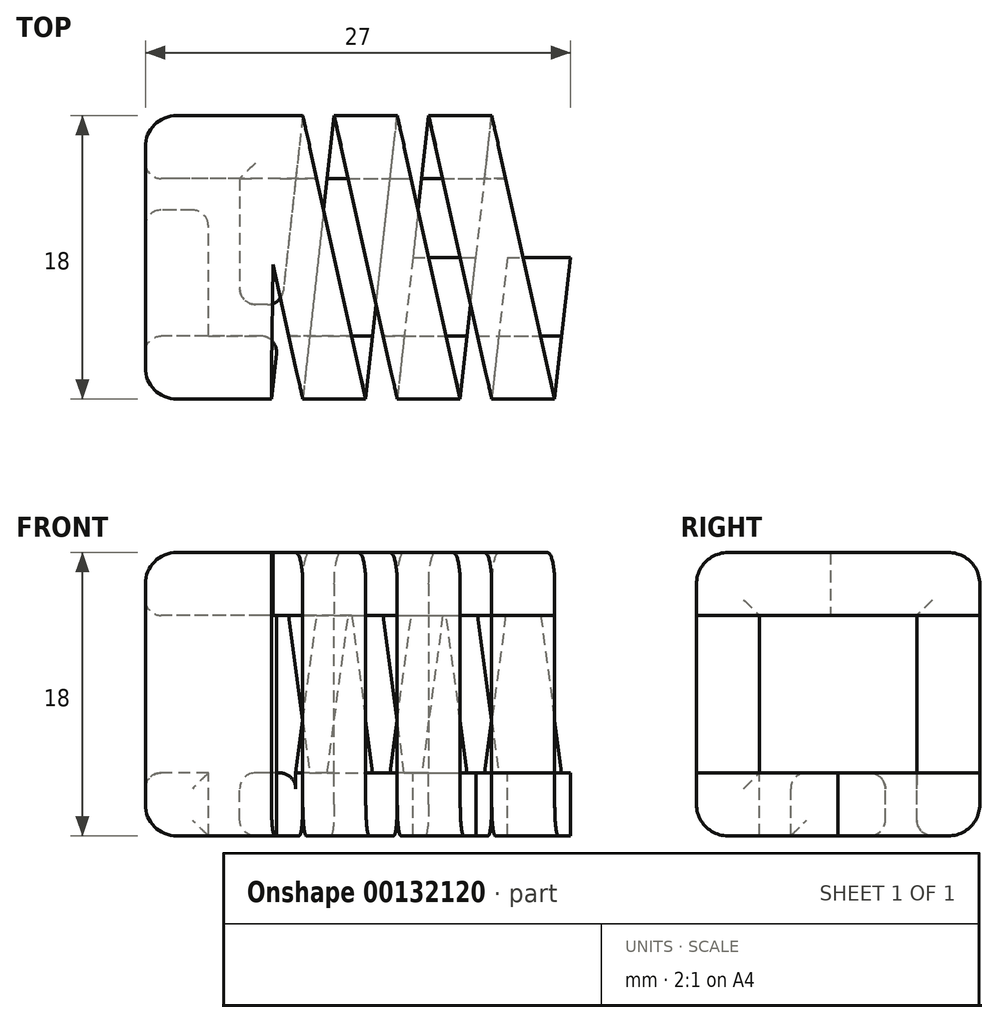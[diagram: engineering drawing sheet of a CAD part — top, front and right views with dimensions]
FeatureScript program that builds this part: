
annotation { "Feature Type Name" : "Feature", "Feature Type Description" : "" }
export const myFeature = defineFeature(function(context is Context, id is Id, definition is map)
    precondition{}
    {
        {
            var Q0;
            Q0=qCreatedBy(makeId("Top.planeOp"),FACE);
            cPlane(context, id + "F0", {"entities" : qUnion([Q0]), "cplaneType" : CPlaneType.OFFSET, "offset" : 10 * mm, "width" : 150 * mm, "height" : 150 * mm});
        }
        {
            var Q0;
            Q0=qCreatedBy(makeId("Top.planeOp"),FACE);
            var sketch = newSketch(context, id + "F1", { "sketchPlane" : qUnion([Q0])});
            skLineSegment(sketch, "E0", {"start": v(0, 0) * mm, "end": v(19.22, 0) * mm, "construction": true});
            skLineSegment(sketch, "E1.0", {"start": v(0, -5) * mm, "end": v(19.22, -5) * mm, "construction": true});
            skLineSegment(sketch, "E2.0", {"start": v(0, 5) * mm, "end": v(19.22, 5) * mm, "construction": true});
            skLineSegment(sketch, "E3.0", {"start": v(0, 9) * mm, "end": v(19.22, 9) * mm, "construction": true});
            skLineSegment(sketch, "E4.0", {"start": v(0, -9) * mm, "end": v(19.22, -9) * mm, "construction": true});
            skLineSegment(sketch, "E5", {"start": v(0, 9) * mm, "end": v(0, -9) * mm, "construction": true});
            skLineSegment(sketch, "E6", {"start": v(0, -9) * mm, "end": v(2, -9) * mm});
            skLineSegment(sketch, "E7", {"start": v(4, 9) * mm, "end": v(2, -9) * mm, "construction": true});
            skLineSegment(sketch, "E8", {"start": v(4, 9) * mm, "end": v(6, 9) * mm, "construction": true});
            skLineSegment(sketch, "E9", {"start": v(6, 9) * mm, "end": v(10, 9) * mm});
            skLineSegment(sketch, "E10", {"start": v(2, -9) * mm, "end": v(4, -9) * mm, "construction": true});
            skLineSegment(sketch, "E11", {"start": v(4, -9) * mm, "end": v(8, -9) * mm});
            skLineSegment(sketch, "E12", {"start": v(6, 9) * mm, "end": v(4, -9) * mm});
            skLineSegment(sketch, "E13", {"start": v(8, -9) * mm, "end": v(10, 9) * mm});
            skLineSegment(sketch, "E14.0", {"start": v(-2, 5) * mm, "end": v(-2, -9) * mm, "construction": true});
            skLineSegment(sketch, "E15.0", {"start": v(-6, 9) * mm, "end": v(-6, -9) * mm, "construction": true});
            skLineSegment(sketch, "E16", {"start": v(0, 5) * mm, "end": v(-6, 5) * mm, "construction": true});
            skLineSegment(sketch, "E17", {"start": v(4, -9) * mm, "end": v(0, -9) * mm, "construction": true});
            skLineSegment(sketch, "E18.0", {"start": v(4, -3) * mm, "end": v(0, -3) * mm, "construction": true});
            skLineSegment(sketch, "E19.0", {"start": v(2, 3) * mm, "end": v(-6, 3) * mm, "construction": true});
            skLineSegment(sketch, "E20", {"start": v(4, 9) * mm, "end": v(2.67, -3) * mm});
            skLineSegment(sketch, "E21", {"start": v(2.67, -3) * mm, "end": v(0, -3) * mm});
            skLineSegment(sketch, "E22", {"start": v(0, 5) * mm, "end": v(0, -3) * mm});
            skLineSegment(sketch, "E23", {"start": v(-6, -9) * mm, "end": v(0, -9) * mm});
            skLineSegment(sketch, "E24", {"start": v(0, -5) * mm, "end": v(-2, -5) * mm});
            skLineSegment(sketch, "E25", {"start": v(-2, -5) * mm, "end": v(-2, 3) * mm});
            skLineSegment(sketch, "E26", {"start": v(-2, 3) * mm, "end": v(-6, 3) * mm});
            skLineSegment(sketch, "E27", {"start": v(0, -5) * mm, "end": v(2.44, -5) * mm});
            skLineSegment(sketch, "E28", {"start": v(2.44, -5) * mm, "end": v(2, -9) * mm});
            skLineSegment(sketch, "E29", {"start": v(-6, 3) * mm, "end": v(-6, -9) * mm});
            skLineSegment(sketch, "E30", {"start": v(-6, 5) * mm, "end": v(-6, 9) * mm});
            skLineSegment(sketch, "E31", {"start": v(0, 5) * mm, "end": v(-6, 5) * mm});
            skLineSegment(sketch, "E32", {"start": v(-6, 9) * mm, "end": v(4, 9) * mm});
            skLineSegment(sketch, "E33", {"start": v(10, 9) * mm, "end": v(12, 9) * mm, "construction": true});
            skLineSegment(sketch, "E34", {"start": v(12, 9) * mm, "end": v(16, 9) * mm});
            skLineSegment(sketch, "E35", {"start": v(8, -9) * mm, "end": v(10, -9) * mm, "construction": true});
            skLineSegment(sketch, "E36", {"start": v(10, -9) * mm, "end": v(14, -9) * mm});
            skLineSegment(sketch, "E37", {"start": v(12, 9) * mm, "end": v(10, -9) * mm});
            skLineSegment(sketch, "E38", {"start": v(14, -9) * mm, "end": v(16, 9) * mm});
            skLineSegment(sketch, "E39", {"start": v(0, 9) * mm, "end": v(0, 5) * mm});
            skLineSegment(sketch, "E40", {"start": v(0, 5) * mm, "end": v(3.56, 5) * mm});
            skLineSegment(sketch, "E41", {"start": v(5.56, 5) * mm, "end": v(9.56, 5) * mm});
            skLineSegment(sketch, "E42", {"start": v(4.44, -5) * mm, "end": v(8.44, -5) * mm});
            skLineSegment(sketch, "E43", {"start": v(11.56, 5) * mm, "end": v(15.56, 5) * mm});
            skLineSegment(sketch, "E44", {"start": v(10.44, -5) * mm, "end": v(14.44, -5) * mm});
            skLineSegment(sketch, "E45", {"start": v(-2, -5) * mm, "end": v(-6, -5) * mm});
            skLineSegment(sketch, "E46", {"start": v(11, 0) * mm, "end": v(15, 0) * mm});
            skPoint(sketch, "E47", {"position": v(13, 0) * mm});
            skPoint(sketch, "E48", {"position": v(-6, 0) * mm});
            skLineSegment(sketch, "E49", {"start": v(5, 0) * mm, "end": v(9, 0) * mm, "construction": true});
            skPoint(sketch, "E50", {"position": v(7, 0) * mm});
            skLineSegment(sketch, "E51", {"start": v(19.22, 9) * mm, "end": v(19.22, -9) * mm});
            skSolve(sketch);
        }
        {
            var Q0;
            Q0=qCreatedBy(id+"F0.planeOp",FACE);
            var sketch = newSketch(context, id + "F2", { "sketchPlane" : qUnion([Q0])});
            skLineSegment(sketch, "E52.0", {"start": v(-6, 9) * mm, "end": v(4, 9) * mm, "construction": true});
            skLineSegment(sketch, "E53.0", {"start": v(-6, 5) * mm, "end": v(-6, 9) * mm, "construction": true});
            skLineSegment(sketch, "E54.0", {"start": v(-6, 9) * mm, "end": v(-6, -9) * mm, "construction": true});
            skLineSegment(sketch, "E55.0", {"start": v(-6, -9) * mm, "end": v(0, -9) * mm, "construction": true});
            skLineSegment(sketch, "E56.0", {"start": v(0, -9) * mm, "end": v(2, -9) * mm, "construction": true});
            skLineSegment(sketch, "E57.0", {"start": v(4, -9) * mm, "end": v(0, -9) * mm, "construction": true});
            skLineSegment(sketch, "E58.0", {"start": v(0, -9) * mm, "end": v(19.22, -9) * mm, "construction": true});
            skLineSegment(sketch, "E59.0", {"start": v(0, 9) * mm, "end": v(19.22, 9) * mm, "construction": true});
            skLineSegment(sketch, "E60.0", {"start": v(14, -9) * mm, "end": v(16, 9) * mm, "construction": true});
            skLineSegment(sketch, "E61.0", {"start": v(12, 9) * mm, "end": v(16, 9) * mm, "construction": true});
            skLineSegment(sketch, "E62.0", {"start": v(12, 9) * mm, "end": v(10, -9) * mm, "construction": true});
            skLineSegment(sketch, "E63.0", {"start": v(10, -9) * mm, "end": v(14, -9) * mm, "construction": true});
            skLineSegment(sketch, "E64.0", {"start": v(8, -9) * mm, "end": v(10, 9) * mm, "construction": true});
            skLineSegment(sketch, "E65.0", {"start": v(4, 9) * mm, "end": v(2.67, -3) * mm, "construction": true});
            skLineSegment(sketch, "E66.0", {"start": v(2.44, -5) * mm, "end": v(2, -9) * mm, "construction": true});
            skLineSegment(sketch, "E67", {"start": v(10, 9) * mm, "end": v(14, -9) * mm});
            skLineSegment(sketch, "E68", {"start": v(10, 9) * mm, "end": v(6, 9) * mm});
            skLineSegment(sketch, "E69", {"start": v(6, 9) * mm, "end": v(10, -9) * mm});
            skLineSegment(sketch, "E70", {"start": v(14, -9) * mm, "end": v(10, -9) * mm});
            skLineSegment(sketch, "E71", {"start": v(4, 9) * mm, "end": v(8, -9) * mm});
            skLineSegment(sketch, "E72", {"start": v(8, -9) * mm, "end": v(4, -9) * mm});
            skLineSegment(sketch, "E73", {"start": v(4, 9) * mm, "end": v(-6, 9) * mm});
            skLineSegment(sketch, "E74", {"start": v(-6, 9) * mm, "end": v(-6, -9) * mm});
            skLineSegment(sketch, "E75", {"start": v(-6, -9) * mm, "end": v(2, -9) * mm});
            skLineSegment(sketch, "E76", {"start": v(2, -9) * mm, "end": v(2.1, -0.47) * mm});
            skPoint(sketch, "E76.endSnap0", {"position": v(2.22, -7) * mm});
            skLineSegment(sketch, "E77", {"start": v(4, -9) * mm, "end": v(2.1, -0.47) * mm});
            skPoint(sketch, "E78.orphan", {"position": v(2.22, 9) * mm});
            skLineSegment(sketch, "E79.0", {"start": v(0, 5) * mm, "end": v(19.22, 5) * mm, "construction": true});
            skLineSegment(sketch, "E80.0", {"start": v(0, -5) * mm, "end": v(19.22, -5) * mm, "construction": true});
            skLineSegment(sketch, "E81", {"start": v(6.89, 5) * mm, "end": v(10.89, 5) * mm});
            skLineSegment(sketch, "E82", {"start": v(9.11, -5) * mm, "end": v(13.11, -5) * mm});
            skLineSegment(sketch, "E83", {"start": v(7.11, -5) * mm, "end": v(3.11, -5) * mm});
            skLineSegment(sketch, "E84", {"start": v(0, 9) * mm, "end": v(0, 5) * mm});
            skLineSegment(sketch, "E85", {"start": v(0, 5) * mm, "end": v(4.89, 5) * mm});
            skLineSegment(sketch, "E86", {"start": v(-30.78, 9) * mm, "end": v(-30.78, -9) * mm, "construction": true});
            skLineSegment(sketch, "E87", {"start": v(19.22, 9) * mm, "end": v(19.22, -9) * mm, "construction": true});
            skSolve(sketch);
        }
        {
            var Q0;
            {var subQ4=sQuery(id+"F1.wireOp",EDGE,"E39");Q0=makeQuery(id+"F1.imprint","IMPRINT",FACE,{"disambiguationData":[TD([[makeQuery(id+"F1.imprint","IMPRINT",EDGE,{"derivedFrom":subQ4}),1.0]])]});}
            var Q1;
            {var subQ0=sQuery(id+"F1.wireOp",EDGE,"E21");Q1=makeQuery(id+"F1.imprint","IMPRINT",FACE,{"disambiguationData":[TD([[makeQuery(id+"F1.imprint","IMPRINT",EDGE,{"derivedFrom":subQ0}),-1.0]])]});}
            var Q2;
            {var subQ0=sQuery(id+"F1.wireOp",EDGE,"E41");Q2=makeQuery(id+"F1.imprint","IMPRINT",FACE,{"disambiguationData":[TD([[makeQuery(id+"F1.imprint","IMPRINT",EDGE,{"derivedFrom":subQ0}),-1.0]])]});}
            var Q3;
            {var subQ0=sQuery(id+"F1.wireOp",EDGE,"E9");Q3=makeQuery(id+"F1.imprint","IMPRINT",FACE,{"disambiguationData":[TD([[makeQuery(id+"F1.imprint","IMPRINT",EDGE,{"derivedFrom":subQ0}),-1.0]])]});}
            var Q4;
            {var subQ0=sQuery(id+"F1.wireOp",EDGE,"E11");Q4=makeQuery(id+"F1.imprint","IMPRINT",FACE,{"disambiguationData":[TD([[makeQuery(id+"F1.imprint","IMPRINT",EDGE,{"derivedFrom":subQ0}),1.0]])]});}
            var Q5;
            {var subQ0=sQuery(id+"F1.wireOp",EDGE,"E36");Q5=makeQuery(id+"F1.imprint","IMPRINT",FACE,{"disambiguationData":[TD([[makeQuery(id+"F1.imprint","IMPRINT",EDGE,{"derivedFrom":subQ0}),1.0]])]});}
            var Q6;
            Q6=makeQuery(id+"F1.imprint","IMPRINT",FACE,{"disambiguationData":[TD([[makeQuery(id+"F1.imprint","IMPRINT",EDGE,{"derivedFrom":sQuery(id+"F1.wireOp",EDGE,"E25")}),1.0]])]});
            var Q7;
            Q7=makeQuery(id+"F1.imprint","IMPRINT",FACE,{"disambiguationData":[TD([[makeQuery(id+"F1.imprint","IMPRINT",EDGE,{"derivedFrom":sQuery(id+"F1.wireOp",EDGE,"E6")}),1.0]])]});
            var Q8;
            {var subQ0=sQuery(id+"F1.wireOp",EDGE,"E30");Q8=makeQuery(id+"F1.imprint","IMPRINT",FACE,{"disambiguationData":[TD([[makeQuery(id+"F1.imprint","IMPRINT",EDGE,{"derivedFrom":subQ0}),-1.0]])]});}
            var Q9;
            {var subQ0=sQuery(id+"F1.wireOp",EDGE,"E44");Q9=makeQuery(id+"F1.imprint","IMPRINT",FACE,{"disambiguationData":[TD([[makeQuery(id+"F1.imprint","IMPRINT",EDGE,{"derivedFrom":subQ0}),1.0]])]});}
            extrude(context, id + "F3", {"entities" : qUnion([Q0, Q1, Q2, Q3, Q4, Q5, Q6, Q7, Q8, Q9]), "oppositeDirection" : true, "depth" : 4 * mm});
        }
        {
            var Q0;
            {var subQ0=sQuery(id+"F2.wireOp",EDGE,"E74");Q0=makeQuery(id+"F2.imprint","IMPRINT",FACE,{"disambiguationData":[TD([[makeQuery(id+"F2.imprint","IMPRINT",EDGE,{"derivedFrom":subQ0}),1.0]])]});}
            var Q1;
            {var subQ4=sQuery(id+"F2.wireOp",EDGE,"E84");Q1=makeQuery(id+"F2.imprint","IMPRINT",FACE,{"disambiguationData":[TD([[makeQuery(id+"F2.imprint","IMPRINT",EDGE,{"derivedFrom":subQ4}),1.0]])]});}
            var Q2;
            {var subQ0=sQuery(id+"F2.wireOp",EDGE,"E68");Q2=makeQuery(id+"F2.imprint","IMPRINT",FACE,{"disambiguationData":[TD([[makeQuery(id+"F2.imprint","IMPRINT",EDGE,{"derivedFrom":subQ0}),1.0]])]});}
            var Q3;
            {var subQ0=sQuery(id+"F2.wireOp",EDGE,"E81");Q3=makeQuery(id+"F2.imprint","IMPRINT",FACE,{"disambiguationData":[TD([[makeQuery(id+"F2.imprint","IMPRINT",EDGE,{"derivedFrom":subQ0}),-1.0]])]});}
            var Q4;
            {var subQ0=sQuery(id+"F2.wireOp",EDGE,"E70");Q4=makeQuery(id+"F2.imprint","IMPRINT",FACE,{"disambiguationData":[TD([[makeQuery(id+"F2.imprint","IMPRINT",EDGE,{"derivedFrom":subQ0}),-1.0]])]});}
            var Q5;
            {var subQ0=sQuery(id+"F2.wireOp",EDGE,"E72");Q5=makeQuery(id+"F2.imprint","IMPRINT",FACE,{"disambiguationData":[TD([[makeQuery(id+"F2.imprint","IMPRINT",EDGE,{"derivedFrom":subQ0}),-1.0]])]});}
            extrude(context, id + "F4", {"entities" : qUnion([Q0, Q1, Q2, Q3, Q4, Q5]), "depth" : 4 * mm});
        }
        {
            var Q0;
            {var subQ0=sQuery(id+"F1.wireOp",EDGE,"E30");Q0=makeQuery(id+"F1.imprint","IMPRINT",FACE,{"disambiguationData":[TD([[makeQuery(id+"F1.imprint","IMPRINT",EDGE,{"derivedFrom":subQ0}),-1.0]])]});}
            var Q1;
            Q1=makeQuery(id+"F1.imprint","IMPRINT",FACE,{"disambiguationData":[TD([[makeQuery(id+"F1.imprint","IMPRINT",EDGE,{"derivedFrom":sQuery(id+"F1.wireOp",EDGE,"E6")}),1.0]])]});
            extrude(context, id + "F5", {"entities" : qUnion([Q0, Q1]), "depth" : 10 * mm});
        }
        {
            var Q0;
            {var subQ0=sQuery(id+"F2.wireOp",EDGE,"E72");Q0=makeQuery(id+"F2.imprint","IMPRINT",FACE,{"disambiguationData":[TD([[makeQuery(id+"F2.imprint","IMPRINT",EDGE,{"derivedFrom":subQ0}),-1.0]])]});}
            var Q1;
            {var subQ0=sQuery(id+"F1.wireOp",EDGE,"E11");Q1=makeQuery(id+"F1.imprint","IMPRINT",FACE,{"disambiguationData":[TD([[makeQuery(id+"F1.imprint","IMPRINT",EDGE,{"derivedFrom":subQ0}),1.0]])]});}
            loft(context, id + "F6", {"sheetProfilesArray" : [{ "sheetProfileEntities" : qUnion([Q0]) }, { "sheetProfileEntities" : qUnion([Q1]) }]});
        }
        {
            var Q0;
            {var subQ0=sQuery(id+"F1.wireOp",EDGE,"E9");Q0=makeQuery(id+"F1.imprint","IMPRINT",FACE,{"disambiguationData":[TD([[makeQuery(id+"F1.imprint","IMPRINT",EDGE,{"derivedFrom":subQ0}),-1.0]])]});}
            var Q1;
            {var subQ0=sQuery(id+"F2.wireOp",EDGE,"E68");Q1=makeQuery(id+"F2.imprint","IMPRINT",FACE,{"disambiguationData":[TD([[makeQuery(id+"F2.imprint","IMPRINT",EDGE,{"derivedFrom":subQ0}),1.0]])]});}
            loft(context, id + "F7", {"sheetProfilesArray" : [{ "sheetProfileEntities" : qUnion([Q0]) }, { "sheetProfileEntities" : qUnion([Q1]) }]});
        }
        {
            var Q0;
            {var subQ0=sQuery(id+"F1.wireOp",EDGE,"E36");Q0=makeQuery(id+"F1.imprint","IMPRINT",FACE,{"disambiguationData":[TD([[makeQuery(id+"F1.imprint","IMPRINT",EDGE,{"derivedFrom":subQ0}),1.0]])]});}
            var Q1;
            {var subQ0=sQuery(id+"F2.wireOp",EDGE,"E70");Q1=makeQuery(id+"F2.imprint","IMPRINT",FACE,{"disambiguationData":[TD([[makeQuery(id+"F2.imprint","IMPRINT",EDGE,{"derivedFrom":subQ0}),-1.0]])]});}
            loft(context, id + "F8", {"sheetProfilesArray" : [{ "sheetProfileEntities" : qUnion([Q0]) }, { "sheetProfileEntities" : qUnion([Q1]) }]});
        }
        {
            var Q0;
            {var subQ4=sQuery(id+"F1.wireOp",EDGE,"E39");Q0=makeQuery(id+"F1.imprint","IMPRINT",FACE,{"disambiguationData":[TD([[makeQuery(id+"F1.imprint","IMPRINT",EDGE,{"derivedFrom":subQ4}),1.0]])]});}
            var Q1;
            {var subQ4=sQuery(id+"F2.wireOp",EDGE,"E84");Q1=makeQuery(id+"F2.imprint","IMPRINT",FACE,{"disambiguationData":[TD([[makeQuery(id+"F2.imprint","IMPRINT",EDGE,{"derivedFrom":subQ4}),1.0]])]});}
            loft(context, id + "F9", {"sheetProfilesArray" : [{ "sheetProfileEntities" : qUnion([Q0]) }, { "sheetProfileEntities" : qUnion([Q1]) }]});
        }
        {
            var Q0;
            Q0=makeQuery(id+"F3.opExtrude","SWEPT_BODY",BODY,{"disambiguationData":[OSD([sQuery(id+"F1.wireOp",EDGE,"E9"),sQuery(id+"F1.wireOp",EDGE,"E11"),sQuery(id+"F1.wireOp",EDGE,"E12"),sQuery(id+"F1.wireOp",EDGE,"E13")])]});
            var Q1;
            Q1=makeQuery(id+"F3.opExtrude","SWEPT_BODY",BODY,{"disambiguationData":[OSD([sQuery(id+"F1.wireOp",EDGE,"E34"),sQuery(id+"F1.wireOp",EDGE,"E36"),sQuery(id+"F1.wireOp",EDGE,"E37"),sQuery(id+"F1.wireOp",EDGE,"E38")])]});
            var Q2;
            Q2=makeQuery(id+"F4.opExtrude","SWEPT_BODY",BODY,{"disambiguationData":[OSD([sQuery(id+"F2.wireOp",EDGE,"E71"),sQuery(id+"F2.wireOp",EDGE,"E72"),sQuery(id+"F2.wireOp",EDGE,"E73"),sQuery(id+"F2.wireOp",EDGE,"E74"),sQuery(id+"F2.wireOp",EDGE,"E75"),sQuery(id+"F2.wireOp",EDGE,"E76"),sQuery(id+"F2.wireOp",EDGE,"E77")])]});
            var Q3;
            Q3=makeQuery(id+"F3.opExtrude","SWEPT_BODY",BODY,{"disambiguationData":[OSD([sQuery(id+"F1.wireOp",EDGE,"E20"),sQuery(id+"F1.wireOp",EDGE,"E21"),sQuery(id+"F1.wireOp",EDGE,"E22"),sQuery(id+"F1.wireOp",EDGE,"E30"),sQuery(id+"F1.wireOp",EDGE,"E31"),sQuery(id+"F1.wireOp",EDGE,"E32")])]});
            var Q4;
            Q4=makeQuery(id+"F4.opExtrude","SWEPT_BODY",BODY,{"disambiguationData":[OSD([sQuery(id+"F2.wireOp",EDGE,"E67"),sQuery(id+"F2.wireOp",EDGE,"E68"),sQuery(id+"F2.wireOp",EDGE,"E69"),sQuery(id+"F2.wireOp",EDGE,"E70")])]});
            var Q5;
            Q5=makeQuery(id+"F3.opExtrude","SWEPT_BODY",BODY,{"disambiguationData":[OSD([sQuery(id+"F1.wireOp",EDGE,"E6"),sQuery(id+"F1.wireOp",EDGE,"E23"),sQuery(id+"F1.wireOp",EDGE,"E24"),sQuery(id+"F1.wireOp",EDGE,"E25"),sQuery(id+"F1.wireOp",EDGE,"E26"),sQuery(id+"F1.wireOp",EDGE,"E27"),sQuery(id+"F1.wireOp",EDGE,"E28"),sQuery(id+"F1.wireOp",EDGE,"E29")])]});
            var Q6;
            {var subQ0=sQuery(id+"F2.wireOp",EDGE,"E70");var subQ4=sQuery(id+"F1.wireOp",EDGE,"E36");Q6=makeQuery(id+"F8.opLoft","SWEPT_BODY",BODY,{"disambiguationData":[OSD([makeQuery(id+"F1.imprint","IMPRINT",FACE,{"disambiguationData":[TD([[makeQuery(id+"F1.imprint","IMPRINT",EDGE,{"derivedFrom":subQ4}),1.0]])]}),makeQuery(id+"F2.imprint","IMPRINT",FACE,{"disambiguationData":[TD([[makeQuery(id+"F2.imprint","IMPRINT",EDGE,{"derivedFrom":subQ0}),-1.0]])]})])]});}
            var Q7;
            {var subQ0=sQuery(id+"F2.wireOp",EDGE,"E72");var subQ4=sQuery(id+"F1.wireOp",EDGE,"E11");Q7=makeQuery(id+"F6.opLoft","SWEPT_BODY",BODY,{"disambiguationData":[OSD([makeQuery(id+"F1.imprint","IMPRINT",FACE,{"disambiguationData":[TD([[makeQuery(id+"F1.imprint","IMPRINT",EDGE,{"derivedFrom":subQ4}),1.0]])]}),makeQuery(id+"F2.imprint","IMPRINT",FACE,{"disambiguationData":[TD([[makeQuery(id+"F2.imprint","IMPRINT",EDGE,{"derivedFrom":subQ0}),-1.0]])]})])]});}
            var Q8;
            {var subQ0=sQuery(id+"F2.wireOp",EDGE,"E68");var subQ4=sQuery(id+"F1.wireOp",EDGE,"E9");Q8=makeQuery(id+"F7.opLoft","SWEPT_BODY",BODY,{"disambiguationData":[OSD([makeQuery(id+"F1.imprint","IMPRINT",FACE,{"disambiguationData":[TD([[makeQuery(id+"F1.imprint","IMPRINT",EDGE,{"derivedFrom":subQ4}),-1.0]])]}),makeQuery(id+"F2.imprint","IMPRINT",FACE,{"disambiguationData":[TD([[makeQuery(id+"F2.imprint","IMPRINT",EDGE,{"derivedFrom":subQ0}),1.0]])]})])]});}
            var Q9;
            Q9=makeQuery(id+"F5.opExtrude","SWEPT_BODY",BODY,{"disambiguationData":[OSD([sQuery(id+"F1.wireOp",EDGE,"E30"),sQuery(id+"F1.wireOp",EDGE,"E31"),sQuery(id+"F1.wireOp",EDGE,"E32"),sQuery(id+"F1.wireOp",EDGE,"E39")])]});
            var Q10;
            {var subQ4=sQuery(id+"F2.wireOp",EDGE,"E84");var subQ9=sQuery(id+"F1.wireOp",EDGE,"E39");Q10=makeQuery(id+"F9.opLoft","SWEPT_BODY",BODY,{"disambiguationData":[OSD([makeQuery(id+"F1.imprint","IMPRINT",FACE,{"disambiguationData":[TD([[makeQuery(id+"F1.imprint","IMPRINT",EDGE,{"derivedFrom":subQ9}),1.0]])]}),makeQuery(id+"F2.imprint","IMPRINT",FACE,{"disambiguationData":[TD([[makeQuery(id+"F2.imprint","IMPRINT",EDGE,{"derivedFrom":subQ4}),1.0]])]})])]});}
            var Q11;
            Q11=makeQuery(id+"F5.opExtrude","SWEPT_BODY",BODY,{"disambiguationData":[OSD([sQuery(id+"F1.wireOp",EDGE,"E6"),sQuery(id+"F1.wireOp",EDGE,"E23"),sQuery(id+"F1.wireOp",EDGE,"E24"),sQuery(id+"F1.wireOp",EDGE,"E27"),sQuery(id+"F1.wireOp",EDGE,"E28"),sQuery(id+"F1.wireOp",EDGE,"E29"),sQuery(id+"F1.wireOp",EDGE,"E45")])]});
            booleanBodies(context, id + "F10", {"operationType" : BooleanOperationType.UNION, "tools" : qUnion([Q0, Q1, Q2, Q3, Q4, Q5, Q6, Q7, Q8, Q9, Q10, Q11])});
        }
        {
            var Q0;
            Q0=makeQuery(id+"F4.opExtrude","CAP_EDGE",EDGE,{"disambiguationData":[OSD([sQuery(id+"F2.wireOp",EDGE,"E68")])],"isStart":false});
            var Q1;
            Q1=makeQuery(id+"F4.opExtrude","CAP_EDGE",EDGE,{"disambiguationData":[OSD([sQuery(id+"F2.wireOp",EDGE,"E73")])],"isStart":false});
            var Q2;
            Q2=makeQuery(id+"F5.opExtrude","SWEPT_EDGE",EDGE,{"disambiguationData":[OSD([sQuery(id+"F1.wireOp",EDGE,"E30"),sQuery(id+"F1.wireOp",EDGE,"E32")])]});
            var Q3;
            Q3=makeQuery(id+"F4.opExtrude","SWEPT_EDGE",EDGE,{"disambiguationData":[OSD([sQuery(id+"F2.wireOp",EDGE,"E73"),sQuery(id+"F2.wireOp",EDGE,"E74")])]});
            var Q4;
            Q4=makeQuery(id+"F4.opExtrude","CAP_EDGE",EDGE,{"disambiguationData":[OSD([sQuery(id+"F2.wireOp",EDGE,"E74")])],"isStart":false});
            var Q5;
            Q5=makeQuery(id+"F4.opExtrude","CAP_EDGE",EDGE,{"disambiguationData":[OSD([sQuery(id+"F2.wireOp",EDGE,"E75")])],"isStart":false});
            var Q6;
            Q6=makeQuery(id+"F4.opExtrude","CAP_EDGE",EDGE,{"disambiguationData":[OSD([sQuery(id+"F2.wireOp",EDGE,"E72")])],"isStart":false});
            var Q7;
            Q7=makeQuery(id+"F4.opExtrude","CAP_EDGE",EDGE,{"disambiguationData":[OSD([sQuery(id+"F2.wireOp",EDGE,"E70")])],"isStart":false});
            var Q8;
            Q8=makeQuery(id+"F5.opExtrude","SWEPT_EDGE",EDGE,{"disambiguationData":[OSD([sQuery(id+"F1.wireOp",EDGE,"E23"),sQuery(id+"F1.wireOp",EDGE,"E29")])]});
            var Q9;
            Q9=makeQuery(id+"F4.opExtrude","SWEPT_EDGE",EDGE,{"disambiguationData":[OSD([sQuery(id+"F2.wireOp",EDGE,"E74"),sQuery(id+"F2.wireOp",EDGE,"E75")])]});
            var Q10;
            Q10=makeQuery(id+"F3.opExtrude","SWEPT_EDGE",EDGE,{"disambiguationData":[OSD([sQuery(id+"F1.wireOp",EDGE,"E30"),sQuery(id+"F1.wireOp",EDGE,"E32")])]});
            var Q11;
            Q11=makeQuery(id+"F3.opExtrude","SWEPT_EDGE",EDGE,{"disambiguationData":[OSD([sQuery(id+"F1.wireOp",EDGE,"E23"),sQuery(id+"F1.wireOp",EDGE,"E29")])]});
            var Q12;
            Q12=makeQuery(id+"F3.opExtrude","CAP_EDGE",EDGE,{"disambiguationData":[OSD([sQuery(id+"F1.wireOp",EDGE,"E29")])],"isStart":false});
            var Q13;
            Q13=makeQuery(id+"F3.opExtrude","CAP_EDGE",EDGE,{"disambiguationData":[OSD([sQuery(id+"F1.wireOp",EDGE,"E30")])],"isStart":false});
            var Q14;
            Q14=makeQuery(id+"F3.opExtrude","CAP_EDGE",EDGE,{"disambiguationData":[OSD([sQuery(id+"F1.wireOp",EDGE,"E6"),sQuery(id+"F1.wireOp",EDGE,"E23")])],"isStart":false});
            var Q15;
            Q15=makeQuery(id+"F3.opExtrude","CAP_EDGE",EDGE,{"disambiguationData":[OSD([sQuery(id+"F1.wireOp",EDGE,"E32")])],"isStart":false});
            var Q16;
            Q16=makeQuery(id+"F3.opExtrude","CAP_EDGE",EDGE,{"disambiguationData":[OSD([sQuery(id+"F1.wireOp",EDGE,"E11")])],"isStart":false});
            var Q17;
            Q17=makeQuery(id+"F3.opExtrude","CAP_EDGE",EDGE,{"disambiguationData":[OSD([sQuery(id+"F1.wireOp",EDGE,"E36")])],"isStart":false});
            var Q18;
            Q18=makeQuery(id+"F3.opExtrude","CAP_EDGE",EDGE,{"disambiguationData":[OSD([sQuery(id+"F1.wireOp",EDGE,"E9")])],"isStart":false});
            fillet(context, id + "F11", {"entities" : qUnion([Q0, Q1, Q2, Q3, Q4, Q5, Q6, Q7, Q8, Q9, Q10, Q11, Q12, Q13, Q14, Q15, Q16, Q17, Q18]), "radius" : 2 * mm, "tangentPropagation" : true, "allowEdgeOverflow" : false});
        }
        {
            var Q0;
            Q0=makeQuery(id+"F3.opExtrude","CAP_EDGE",EDGE,{"disambiguationData":[OSD([sQuery(id+"F1.wireOp",EDGE,"E29")])],"isStart":true});
            var Q1;
            Q1=makeQuery(id+"F5.opExtrude","SWEPT_EDGE",EDGE,{"disambiguationData":[OSD([sQuery(id+"F1.wireOp",EDGE,"E29"),sQuery(id+"F1.wireOp",EDGE,"E45")])]});
            var Q2;
            Q2=makeQuery(id+"F4.opExtrude","CAP_EDGE",EDGE,{"disambiguationData":[OSD([sQuery(id+"F2.wireOp",EDGE,"E74")])],"isStart":true});
            var Q3;
            {var subQ0=sQuery(id+"F1.wireOp",EDGE,"E31");var subQ1=sQuery(id+"F1.wireOp",EDGE,"E30");Q3=makeQuery(id+"F10.opBoolean","MERGE",EDGE,{"derivedFrom":[makeQuery(id+"F3.opExtrude","SWEPT_EDGE",EDGE,{"disambiguationData":[OSD([subQ1,subQ0])]}),makeQuery(id+"F5.opExtrude","SWEPT_EDGE",EDGE,{"disambiguationData":[OSD([subQ1,subQ0])]})]});}
            var Q4;
            Q4=makeQuery(id+"F3.opExtrude","SWEPT_EDGE",EDGE,{"disambiguationData":[OSD([sQuery(id+"F1.wireOp",EDGE,"E26"),sQuery(id+"F1.wireOp",EDGE,"E29")])]});
            var Q5;
            Q5=makeQuery(id+"F3.opExtrude","CAP_EDGE",EDGE,{"disambiguationData":[OSD([sQuery(id+"F1.wireOp",EDGE,"E26")])],"isStart":true});
            var Q6;
            Q6=makeQuery(id+"F3.opExtrude","SWEPT_EDGE",EDGE,{"disambiguationData":[OSD([sQuery(id+"F1.wireOp",EDGE,"E25"),sQuery(id+"F1.wireOp",EDGE,"E26")])]});
            var Q7;
            Q7=makeQuery(id+"F3.opExtrude","CAP_EDGE",EDGE,{"disambiguationData":[OSD([sQuery(id+"F1.wireOp",EDGE,"E22")])],"isStart":true});
            var Q8;
            Q8=makeQuery(id+"F3.opExtrude","CAP_EDGE",EDGE,{"disambiguationData":[OSD([sQuery(id+"F1.wireOp",EDGE,"E22")])],"isStart":false});
            var Q9;
            Q9=makeQuery(id+"F3.opExtrude","CAP_EDGE",EDGE,{"disambiguationData":[OSD([sQuery(id+"F1.wireOp",EDGE,"E21")])],"isStart":true});
            var Q10;
            Q10=makeQuery(id+"F10.opBoolean","SPLIT",EDGE,{"derivedFrom":makeQuery(id+"F3.opExtrude","CAP_EDGE",EDGE,{"disambiguationData":[OSD([sQuery(id+"F1.wireOp",EDGE,"E20")])],"isStart":true})});
            var Q11;
            Q11=makeQuery(id+"F3.opExtrude","SWEPT_EDGE",EDGE,{"disambiguationData":[OSD([sQuery(id+"F1.wireOp",EDGE,"E20"),sQuery(id+"F1.wireOp",EDGE,"E21")])]});
            var Q12;
            Q12=makeQuery(id+"F3.opExtrude","SWEPT_EDGE",EDGE,{"disambiguationData":[OSD([sQuery(id+"F1.wireOp",EDGE,"E21"),sQuery(id+"F1.wireOp",EDGE,"E22")])]});
            var Q13;
            {var subQ0=sQuery(id+"F1.wireOp",EDGE,"E28");var subQ1=sQuery(id+"F1.wireOp",EDGE,"E27");Q13=makeQuery(id+"F10.opBoolean","MERGE",EDGE,{"derivedFrom":[makeQuery(id+"F3.opExtrude","SWEPT_EDGE",EDGE,{"disambiguationData":[OSD([subQ1,subQ0])]}),makeQuery(id+"F5.opExtrude","SWEPT_EDGE",EDGE,{"disambiguationData":[OSD([subQ1,subQ0])]})]});}
            fillet(context, id + "F12", {"entities" : qUnion([Q0, Q1, Q2, Q3, Q4, Q5, Q6, Q7, Q8, Q9, Q10, Q11, Q12, Q13]), "radius" : 1 * mm, "tangentPropagation" : true, "allowEdgeOverflow" : false});
        }
        {
            var Q0;
            Q0=qCreatedBy(makeId("Top.planeOp"),FACE);
            var sketch = newSketch(context, id + "F13", { "sketchPlane" : qUnion([Q0])});
            skLineSegment(sketch, "E88.0", {"start": v(0, 9) * mm, "end": v(19.22, 9) * mm, "construction": true});
            skLineSegment(sketch, "E88.1", {"start": v(0, 5) * mm, "end": v(19.22, 5) * mm, "construction": true});
            skLineSegment(sketch, "E89.0", {"start": v(14, -9) * mm, "end": v(16, 9) * mm, "construction": true});
            skLineSegment(sketch, "E90.0", {"start": v(0, -5) * mm, "end": v(19.22, -5) * mm, "construction": true});
            skLineSegment(sketch, "E91.0", {"start": v(0, -9) * mm, "end": v(19.22, -9) * mm, "construction": true});
            skLineSegment(sketch, "E92", {"start": v(16, 9) * mm, "end": v(18, 9) * mm, "construction": true});
            skLineSegment(sketch, "E93", {"start": v(18, 9) * mm, "end": v(22, 9) * mm});
            skLineSegment(sketch, "E94", {"start": v(14, -9) * mm, "end": v(16, -9) * mm, "construction": true});
            skLineSegment(sketch, "E95", {"start": v(16, -9) * mm, "end": v(20, -9) * mm});
            skLineSegment(sketch, "E96", {"start": v(18, 9) * mm, "end": v(16, -9) * mm});
            skLineSegment(sketch, "E97", {"start": v(20, -9) * mm, "end": v(22, 9) * mm});
            skLineSegment(sketch, "E98", {"start": v(17.56, 5) * mm, "end": v(21.56, 5) * mm});
            skLineSegment(sketch, "E99", {"start": v(16.44, -5) * mm, "end": v(20.44, -5) * mm});
            skLineSegment(sketch, "E100", {"start": v(17, 0) * mm, "end": v(21, 0) * mm});
            skLineSegment(sketch, "E101.0", {"start": v(12, 9) * mm, "end": v(10, -9) * mm, "construction": true});
            skLineSegment(sketch, "E102", {"start": v(15, 0) * mm, "end": v(11, 0) * mm, "construction": true});
            skSolve(sketch);
        }
        {
            var Q0;
            Q0=qCreatedBy(id+"F0.planeOp",FACE);
            var sketch = newSketch(context, id + "F14", { "sketchPlane" : qUnion([Q0])});
            skLineSegment(sketch, "E103.0", {"start": v(0, 5) * mm, "end": v(19.22, 5) * mm, "construction": true});
            skLineSegment(sketch, "E104.0", {"start": v(0, 9) * mm, "end": v(19.22, 9) * mm, "construction": true});
            skLineSegment(sketch, "E105.0", {"start": v(0, -5) * mm, "end": v(19.22, -5) * mm, "construction": true});
            skLineSegment(sketch, "E106.0", {"start": v(0, -9) * mm, "end": v(19.22, -9) * mm, "construction": true});
            skLineSegment(sketch, "E107.0", {"start": v(20, -9) * mm, "end": v(22, 9) * mm, "construction": true});
            skLineSegment(sketch, "E108.0", {"start": v(18, 9) * mm, "end": v(16, -9) * mm, "construction": true});
            skLineSegment(sketch, "E109.0", {"start": v(14, -9) * mm, "end": v(16, 9) * mm, "construction": true});
            skLineSegment(sketch, "E110.0", {"start": v(12, 9) * mm, "end": v(10, -9) * mm, "construction": true});
            skLineSegment(sketch, "E111", {"start": v(12, 9) * mm, "end": v(16, -9) * mm});
            skLineSegment(sketch, "E112", {"start": v(20, -9) * mm, "end": v(16, 9) * mm});
            skLineSegment(sketch, "E113", {"start": v(16, 9) * mm, "end": v(12, 9) * mm});
            skLineSegment(sketch, "E114", {"start": v(16, -9) * mm, "end": v(20, -9) * mm});
            skLineSegment(sketch, "E115", {"start": v(15.11, -5) * mm, "end": v(19.11, -5) * mm});
            skLineSegment(sketch, "E116", {"start": v(12.89, 5) * mm, "end": v(16.89, 5) * mm});
            skSolve(sketch);
        }
        {
            var Q0;
            {var subQ0=sQuery(id+"F14.wireOp",EDGE,"E113");Q0=makeQuery(id+"F14.imprint","IMPRINT",FACE,{"disambiguationData":[TD([[makeQuery(id+"F14.imprint","IMPRINT",EDGE,{"derivedFrom":subQ0}),1.0]])]});}
            var Q1;
            {var subQ0=sQuery(id+"F14.wireOp",EDGE,"E115");Q1=makeQuery(id+"F14.imprint","IMPRINT",FACE,{"disambiguationData":[TD([[makeQuery(id+"F14.imprint","IMPRINT",EDGE,{"derivedFrom":subQ0}),1.0]])]});}
            var Q2;
            {var subQ0=sQuery(id+"F14.wireOp",EDGE,"E114");Q2=makeQuery(id+"F14.imprint","IMPRINT",FACE,{"disambiguationData":[TD([[makeQuery(id+"F14.imprint","IMPRINT",EDGE,{"derivedFrom":subQ0}),1.0]])]});}
            extrude(context, id + "F15", {"entities" : qUnion([Q0, Q1, Q2]), "depth" : 4 * mm});
        }
        {
            var Q0;
            {var subQ0=sQuery(id+"F13.wireOp",EDGE,"E95");Q0=makeQuery(id+"F13.imprint","IMPRINT",FACE,{"disambiguationData":[TD([[makeQuery(id+"F13.imprint","IMPRINT",EDGE,{"derivedFrom":subQ0}),1.0]])]});}
            var Q1;
            {var subQ0=sQuery(id+"F1.wireOp",EDGE,"E43");Q1=makeQuery(id+"F1.imprint","IMPRINT",FACE,{"disambiguationData":[TD([[makeQuery(id+"F1.imprint","IMPRINT",EDGE,{"derivedFrom":subQ0}),-1.0]])]});}
            var Q2;
            {var subQ0=sQuery(id+"F1.wireOp",EDGE,"E34");Q2=makeQuery(id+"F1.imprint","IMPRINT",FACE,{"disambiguationData":[TD([[makeQuery(id+"F1.imprint","IMPRINT",EDGE,{"derivedFrom":subQ0}),-1.0]])]});}
            var Q3;
            {var subQ0=sQuery(id+"F13.wireOp",EDGE,"E99");Q3=makeQuery(id+"F13.imprint","IMPRINT",FACE,{"disambiguationData":[TD([[makeQuery(id+"F13.imprint","IMPRINT",EDGE,{"derivedFrom":subQ0}),1.0]])]});}
            extrude(context, id + "F16", {"entities" : qUnion([Q0, Q1, Q2, Q3]), "oppositeDirection" : true, "depth" : 4 * mm});
        }
        {
            var Q1;
            {var subQ0=sQuery(id+"F14.wireOp",EDGE,"E113");Q1=makeQuery(id+"F14.imprint","IMPRINT",FACE,{"disambiguationData":[TD([[makeQuery(id+"F14.imprint","IMPRINT",EDGE,{"derivedFrom":subQ0}),1.0]])]});}
            var Q2;
            {var subQ0=sQuery(id+"F1.wireOp",EDGE,"E34");Q2=makeQuery(id+"F1.imprint","IMPRINT",FACE,{"disambiguationData":[TD([[makeQuery(id+"F1.imprint","IMPRINT",EDGE,{"derivedFrom":subQ0}),-1.0]])]});}
            loft(context, id + "F17", {"operationType" : NewBodyOperationType.ADD, "sheetProfilesArray" : [{ "sheetProfileEntities" : qUnion([Q1]) }, { "sheetProfileEntities" : qUnion([Q2]) }]});
        }
        {
            var Q0;
            {var subQ0=sQuery(id+"F14.wireOp",EDGE,"E114");Q0=makeQuery(id+"F14.imprint","IMPRINT",FACE,{"disambiguationData":[TD([[makeQuery(id+"F14.imprint","IMPRINT",EDGE,{"derivedFrom":subQ0}),1.0]])]});}
            var Q1;
            {var subQ0=sQuery(id+"F13.wireOp",EDGE,"E95");Q1=makeQuery(id+"F13.imprint","IMPRINT",FACE,{"disambiguationData":[TD([[makeQuery(id+"F13.imprint","IMPRINT",EDGE,{"derivedFrom":subQ0}),1.0]])]});}
            loft(context, id + "F18", {"sheetProfilesArray" : [{ "sheetProfileEntities" : qUnion([Q0]) }, { "sheetProfileEntities" : qUnion([Q1]) }]});
        }
        {
            var Q0;
            Q0=makeQuery(id+"F15.opExtrude","CAP_EDGE",EDGE,{"disambiguationData":[OSD([sQuery(id+"F14.wireOp",EDGE,"E114")])],"isStart":false});
            var Q1;
            Q1=makeQuery(id+"F16.opExtrude","CAP_EDGE",EDGE,{"disambiguationData":[OSD([sQuery(id+"F13.wireOp",EDGE,"E95")])],"isStart":false});
            var Q2;
            Q2=makeQuery(id+"F15.opExtrude","CAP_EDGE",EDGE,{"disambiguationData":[OSD([sQuery(id+"F14.wireOp",EDGE,"E113")])],"isStart":false});
            var Q3;
            Q3=makeQuery(id+"F16.opExtrude","CAP_EDGE",EDGE,{"disambiguationData":[OSD([sQuery(id+"F13.wireOp",EDGE,"E93")])],"isStart":false});
            var Q4;
            Q4=makeQuery(id+"F16.opExtrude","CAP_EDGE",EDGE,{"disambiguationData":[OSD([sQuery(id+"F1.wireOp",EDGE,"E34")])],"isStart":false});
            fillet(context, id + "F19", {"entities" : qUnion([Q0, Q1, Q2, Q3, Q4]), "radius" : 2 * mm, "tangentPropagation" : true, "allowEdgeOverflow" : false});
        }
    });
